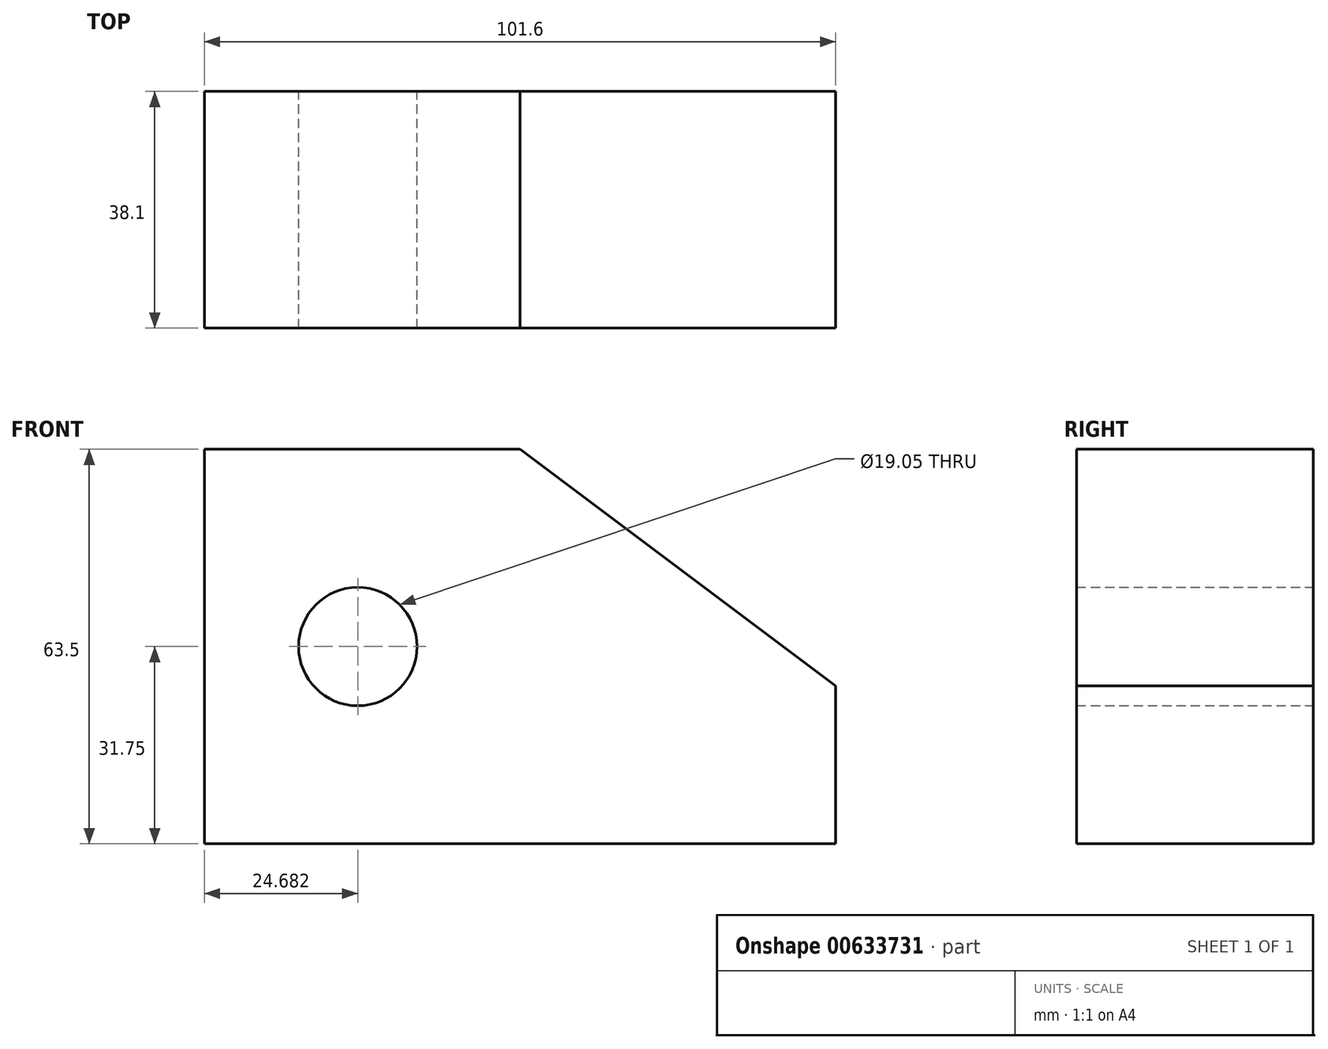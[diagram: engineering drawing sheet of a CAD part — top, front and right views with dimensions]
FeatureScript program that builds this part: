
annotation { "Feature Type Name" : "Feature", "Feature Type Description" : "" }
export const myFeature = defineFeature(function(context is Context, id is Id, definition is map)
    precondition{}
    {
        {
            var Q0;
            Q0=qCreatedBy(makeId("Front.planeOp"),FACE);
            var sketch = newSketch(context, id + "F0", { "sketchPlane" : qUnion([Q0])});
            skLineSegment(sketch, "E0", {"start": v(0, 0) * mm, "end": v(101.6, 0) * mm});
            skLineSegment(sketch, "E1", {"start": v(101.6, 0) * mm, "end": v(101.6, 25.4) * mm});
            skLineSegment(sketch, "E2", {"start": v(101.6, 25.4) * mm, "end": v(50.8, 63.5) * mm});
            skLineSegment(sketch, "E3", {"start": v(50.8, 63.5) * mm, "end": v(0, 63.5) * mm});
            skLineSegment(sketch, "E4", {"start": v(0, 63.5) * mm, "end": v(0, 0) * mm});
            skCircle(sketch, "E5", {"center": v(24.68, 31.75) * mm, "radius": 9.53 * mm});
            skSolve(sketch);
        }
        {
            var Q0;
            Q0=makeQuery(id+"F0.imprint","IMPRINT",FACE,{"disambiguationData":[TD([[makeQuery(id+"F0.imprint","IMPRINT",EDGE,{"derivedFrom":sQuery(id+"F0.wireOp",EDGE,"E0")}),1.0]])]});
            extrude(context, id + "F1", {"entities" : qUnion([Q0]), "depth" : 38.1 * mm, "offsetDistance" : 25.4 * mm});
        }
    });
